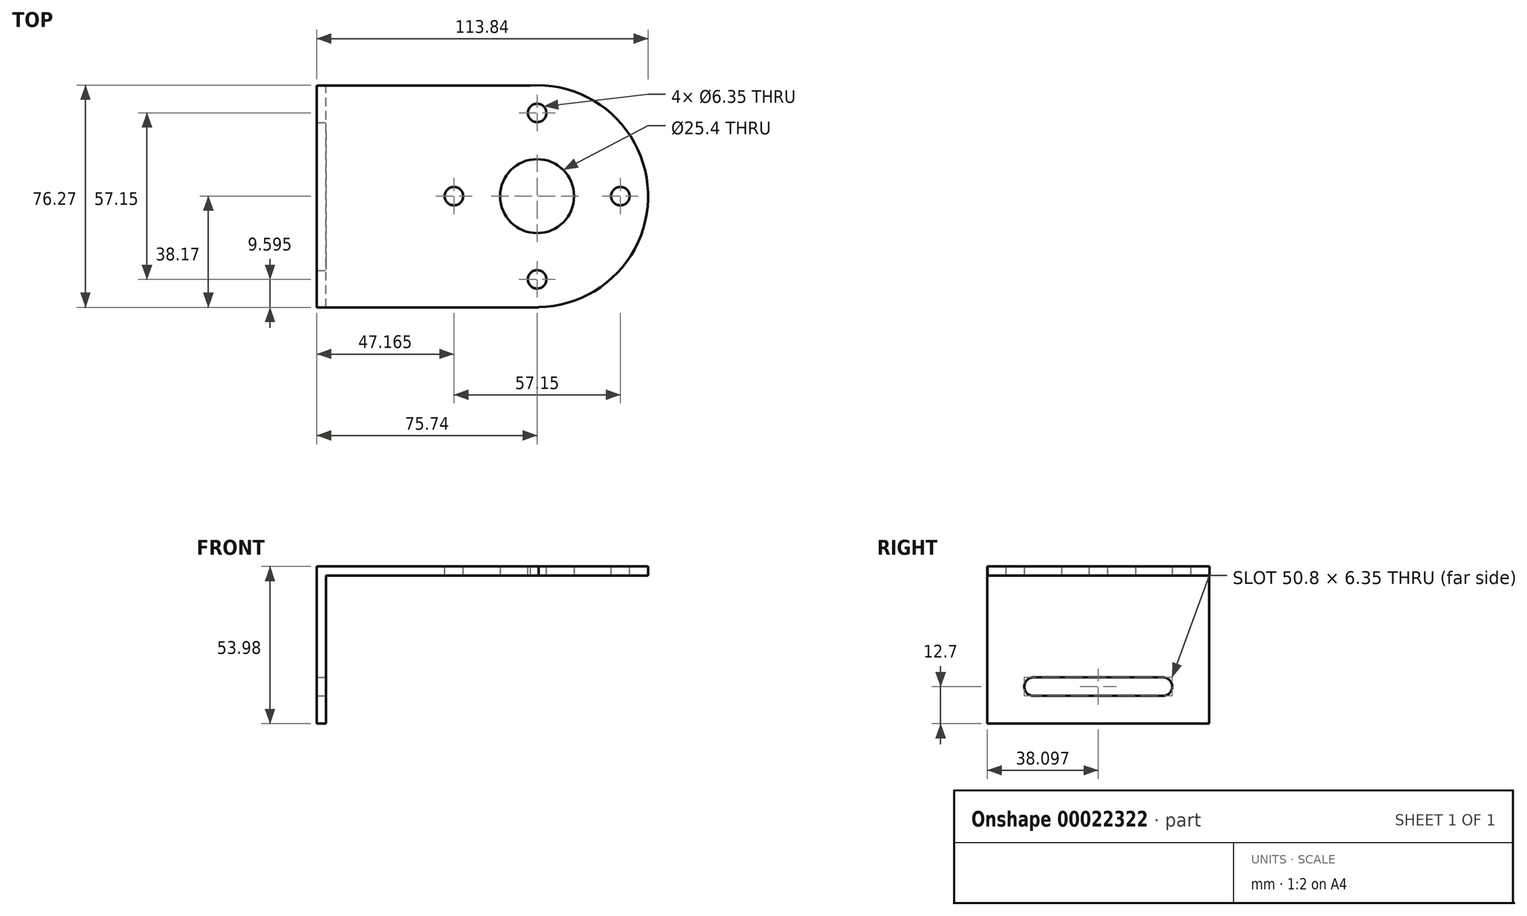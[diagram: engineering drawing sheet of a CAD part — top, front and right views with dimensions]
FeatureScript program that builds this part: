
annotation { "Feature Type Name" : "Feature", "Feature Type Description" : "" }
export const myFeature = defineFeature(function(context is Context, id is Id, definition is map)
    precondition{}
    {
        {
            var Q0;
            Q0=qCreatedBy(makeId("Top.planeOp"),FACE);
            var sketch = newSketch(context, id + "F0", { "sketchPlane" : qUnion([Q0])});
            skLineSegment(sketch, "E0.bottom", {"start": v(-75.74, 38.03) * mm, "end": v(0.46, 38.03) * mm});
            skLineSegment(sketch, "E0.top", {"start": v(-75.74, -38.17) * mm, "end": v(0.46, -38.17) * mm});
            skLineSegment(sketch, "E0.left", {"start": v(-75.74, 38.03) * mm, "end": v(-75.74, -38.17) * mm});
            skLineSegment(sketch, "E0.right", {"start": v(0.46, 38.03) * mm, "end": v(0.46, -38.17) * mm});
            skCircle(sketch, "E1", {"center": v(0, 0) * mm, "radius": 38.1 * mm});
            skLineSegment(sketch, "E2.bottom", {"start": v(-75.74, 38.03) * mm, "end": v(-75.74, 38.03) * mm});
            skLineSegment(sketch, "E2.top", {"start": v(-75.74, -38.17) * mm, "end": v(-75.74, -38.17) * mm});
            skPoint(sketch, "E3.rect.middle", {"position": v(-75.74, -38.17) * mm});
            skPoint(sketch, "E4.rect.middle", {"position": v(-75.74, 0) * mm});
            skSolve(sketch);
        }
        {
            var Q0;
            Q0 = qSketchRegion(id + "F0", true);
            extrude(context, id + "F1", {"entities" : qUnion([Q0]), "depth" : 3.17 * mm});
        }
        {
            var Q0;
            Q0=makeQuery(id+"F1.opExtrude","CAP_FACE",FACE,{"disambiguationData":[OSD([sQuery(id+"F0.wireOp",EDGE,"E0.bottom"),sQuery(id+"F0.wireOp",EDGE,"E0.top"),sQuery(id+"F0.wireOp",EDGE,"E0.right"),sQuery(id+"F0.wireOp",EDGE,"E1"),sQuery(id+"F0.wireOp",EDGE,"E0.left")])],"isStart":true});
            var sketch = newSketch(context, id + "F2", { "sketchPlane" : qUnion([Q0])});
            skLineSegment(sketch, "E5", {"start": v(-72.57, 38.17) * mm, "end": v(-72.57, -38.03) * mm});
            skSolve(sketch);
        }
        {
            var Q0;
            {var subQ1=sQuery(id+"F2.wireOp",EDGE,"E5");Q0=makeQuery(id+"F2.imprint","IMPRINT",FACE,{"disambiguationData":[TD([[makeQuery(id+"F2.imprint","IMPRINT",EDGE,{"derivedFrom":subQ1}),-1.0]])]});}
            extrude(context, id + "F3", {"entities" : qUnion([Q0]), "operationType" : NewBodyOperationType.ADD, "depth" : 50.8 * mm});
        }
        {
            var Q0;
            Q0=makeQuery(id+"F1.opExtrude","CAP_FACE",FACE,{"disambiguationData":[OSD([sQuery(id+"F0.wireOp",EDGE,"E0.bottom"),sQuery(id+"F0.wireOp",EDGE,"E0.top"),sQuery(id+"F0.wireOp",EDGE,"E0.right"),sQuery(id+"F0.wireOp",EDGE,"E1"),sQuery(id+"F0.wireOp",EDGE,"E0.left")])],"isStart":true});
            var sketch = newSketch(context, id + "F4", { "sketchPlane" : qUnion([Q0])});
            skCircle(sketch, "E6", {"center": v(0, 0) * mm, "radius": 12.7 * mm});
            skSolve(sketch);
        }
        {
            var Q0;
            Q0=makeQuery(id+"F4.imprint","IMPRINT",FACE,{"disambiguationData":[TD([[makeQuery(id+"F4.imprint","IMPRINT",EDGE,{"derivedFrom":sQuery(id+"F4.wireOp",EDGE,"E6")}),1.0]])]});
            extrude(context, id + "F5", {"entities" : qUnion([Q0]), "operationType" : NewBodyOperationType.REMOVE, "oppositeDirection" : true, "depth" : 3.2 * mm});
        }
        {
            var Q0;
            Q0=makeQuery(id+"F1.opExtrude","CAP_FACE",FACE,{"disambiguationData":[OSD([sQuery(id+"F0.wireOp",EDGE,"E0.bottom"),sQuery(id+"F0.wireOp",EDGE,"E0.top"),sQuery(id+"F0.wireOp",EDGE,"E0.right"),sQuery(id+"F0.wireOp",EDGE,"E1"),sQuery(id+"F0.wireOp",EDGE,"E0.left")])],"isStart":false});
            var sketch = newSketch(context, id + "F6", { "sketchPlane" : qUnion([Q0])});
            skCircle(sketch, "E7", {"center": v(0, 0) * mm, "radius": 28.58 * mm, "construction": true});
            skCircle(sketch, "E8", {"center": v(-28.58, 0) * mm, "radius": 3.18 * mm});
            skCircle(sketch, "E9.1.0", {"center": v(0, -28.58) * mm, "radius": 3.18 * mm});
            skCircle(sketch, "E9.2.0", {"center": v(28.58, 0) * mm, "radius": 3.18 * mm});
            skCircle(sketch, "E9.3.0", {"center": v(0, 28.58) * mm, "radius": 3.18 * mm});
            skSolve(sketch);
        }
        {
            var Q0;
            Q0 = qSketchRegion(id + "F6", true);
            extrude(context, id + "F7", {"entities" : qUnion([Q0]), "operationType" : NewBodyOperationType.REMOVE, "oppositeDirection" : true, "depth" : 25.4 * mm});
        }
        {
            var Q0;
            Q0=makeQuery(id+"F3.opExtrude","SWEPT_FACE",FACE,{"disambiguationData":[OSD([sQuery(id+"F2.wireOp",EDGE,"E5")])]});
            var sketch = newSketch(context, id + "F8", { "sketchPlane" : qUnion([Q0])});
            skLineSegment(sketch, "E10", {"start": v(38.03, -38.1) * mm, "end": v(-38.17, -38.1) * mm, "construction": true});
            skLineSegment(sketch, "E11", {"start": v(22.15, -50.8) * mm, "end": v(22.15, 0) * mm, "construction": true});
            skLineSegment(sketch, "E12", {"start": v(-22.3, -50.8) * mm, "end": v(-22.3, 0) * mm, "construction": true});
            skCircle(sketch, "E13", {"center": v(22.15, -38.1) * mm, "radius": 3.18 * mm});
            skCircle(sketch, "E14", {"center": v(-22.3, -38.1) * mm, "radius": 3.18 * mm});
            skLineSegment(sketch, "E15", {"start": v(22.15, -41.28) * mm, "end": v(-22.3, -41.28) * mm});
            skLineSegment(sketch, "E16", {"start": v(22.15, -34.92) * mm, "end": v(-22.3, -34.92) * mm});
            skSolve(sketch);
        }
        {
            var Q0;
            {var subQ0=sQuery(id+"F8.wireOp",EDGE,"E14");var subQ2=makeQuery(id+"F8.imprint","INTERSECT",VERTEX,{"derivedFrom":[subQ0,sQuery(id+"F8.wireOp",EDGE,"E15")]});Q0=makeQuery(id+"F8.imprint","IMPRINT",FACE,{"disambiguationData":[TD([[makeQuery(id+"F8.imprint","IMPRINT",EDGE,{"disambiguationData":[TD([[subQ2,1.0]])],"derivedFrom":subQ0}),1.0]])]});}
            var Q1;
            {var subQ1=sQuery(id+"F8.wireOp",EDGE,"E15");Q1=makeQuery(id+"F8.imprint","IMPRINT",FACE,{"disambiguationData":[TD([[makeQuery(id+"F8.imprint","IMPRINT",EDGE,{"derivedFrom":subQ1}),-1.0]])]});}
            var Q2;
            {var subQ0=sQuery(id+"F8.wireOp",EDGE,"E13");var subQ2=makeQuery(id+"F8.imprint","INTERSECT",VERTEX,{"derivedFrom":[subQ0,sQuery(id+"F8.wireOp",EDGE,"E15")]});Q2=makeQuery(id+"F8.imprint","IMPRINT",FACE,{"disambiguationData":[TD([[makeQuery(id+"F8.imprint","IMPRINT",EDGE,{"disambiguationData":[TD([[subQ2,1.0]])],"derivedFrom":subQ0}),1.0]])]});}
            extrude(context, id + "F9", {"entities" : qUnion([Q0, Q1, Q2]), "operationType" : NewBodyOperationType.REMOVE, "oppositeDirection" : true, "depth" : 3.17 * mm});
        }
    });
